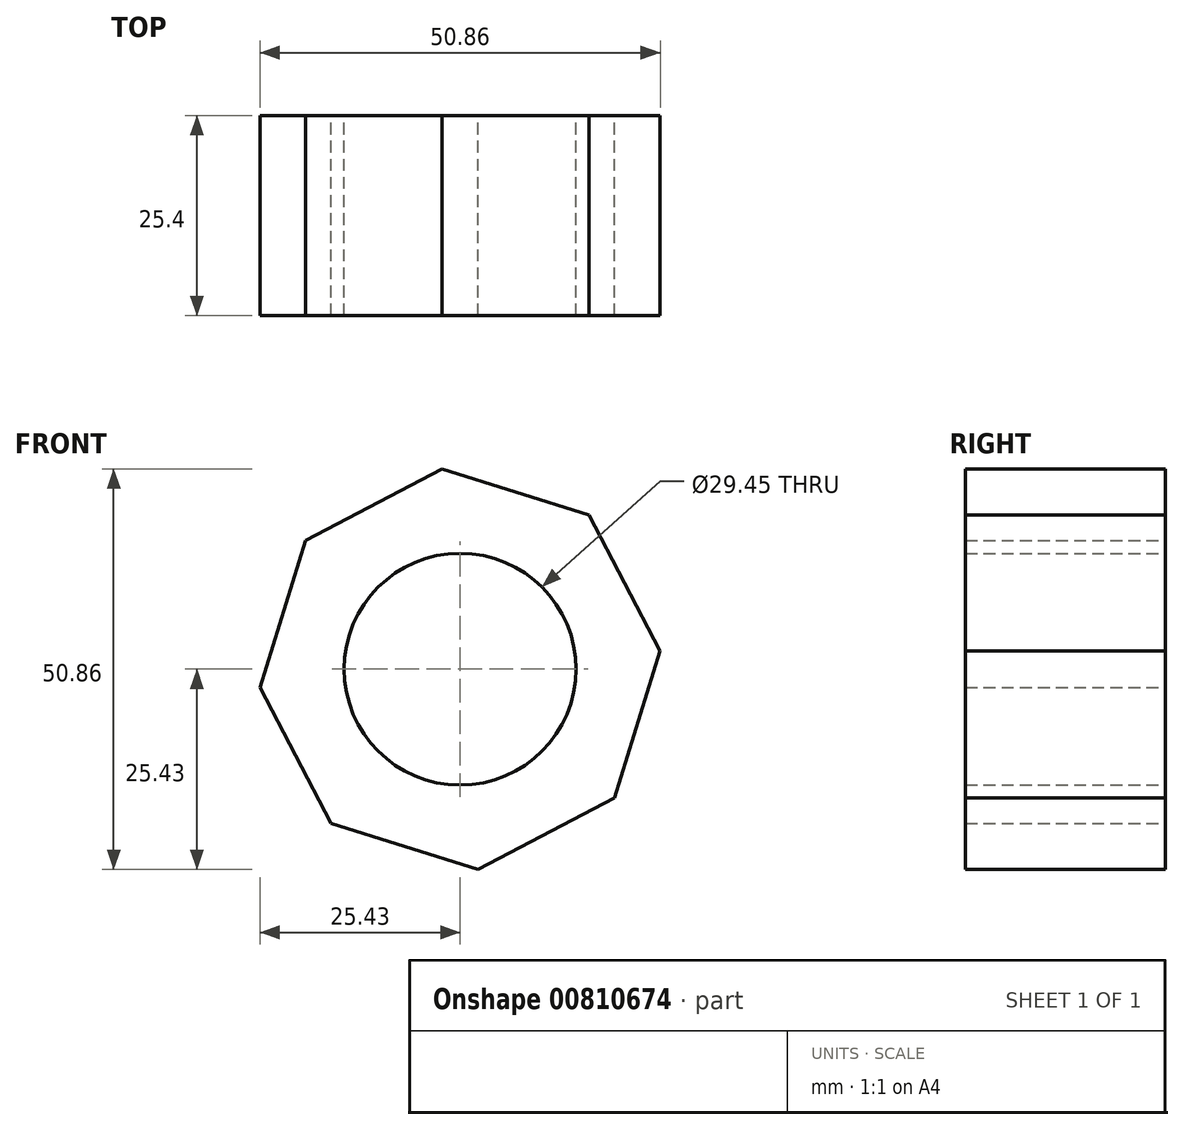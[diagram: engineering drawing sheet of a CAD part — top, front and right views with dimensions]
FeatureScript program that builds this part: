
annotation { "Feature Type Name" : "Feature", "Feature Type Description" : "" }
export const myFeature = defineFeature(function(context is Context, id is Id, definition is map)
    precondition{}
    {
        {
            var Q0;
            Q0=qCreatedBy(makeId("Front.planeOp"),FACE);
            var sketch = newSketch(context, id + "F0", { "sketchPlane" : qUnion([Q0])});
            skCircle(sketch, "E0.cCircle", {"center": v(0, 0) * mm, "radius": 23.59 * mm, "construction": true});
            skLineSegment(sketch, "E0.0", {"start": v(-25.43, -2.3) * mm, "end": v(-19.6, 16.35) * mm});
            skLineSegment(sketch, "E0.1", {"start": v(-19.6, 16.35) * mm, "end": v(-2.3, 25.43) * mm});
            skLineSegment(sketch, "E0.2", {"start": v(-2.3, 25.43) * mm, "end": v(16.35, 19.6) * mm});
            skLineSegment(sketch, "E0.3", {"start": v(16.35, 19.6) * mm, "end": v(25.43, 2.3) * mm});
            skLineSegment(sketch, "E0.4", {"start": v(25.43, 2.3) * mm, "end": v(19.6, -16.35) * mm});
            skLineSegment(sketch, "E0.5", {"start": v(19.6, -16.35) * mm, "end": v(2.3, -25.43) * mm});
            skLineSegment(sketch, "E0.6", {"start": v(2.3, -25.43) * mm, "end": v(-16.35, -19.6) * mm});
            skLineSegment(sketch, "E0.7", {"start": v(-16.35, -19.6) * mm, "end": v(-25.43, -2.3) * mm});
            skPoint(sketch, "E0.0.midPoint", {"position": v(-22.52, 7.03) * mm});
            skCircle(sketch, "E1", {"center": v(0, 0) * mm, "radius": 14.73 * mm});
            skSolve(sketch);
        }
        {
            var Q0;
            Q0=qSketchRegion(id+"F0",true);
            extrude(context, id + "F1", {"entities" : qUnion([Q0]), "endBound" : BoundingType.SYMMETRIC, "depth" : 25.4 * mm, "offsetDistance" : 25.4 * mm});
        }
    });
